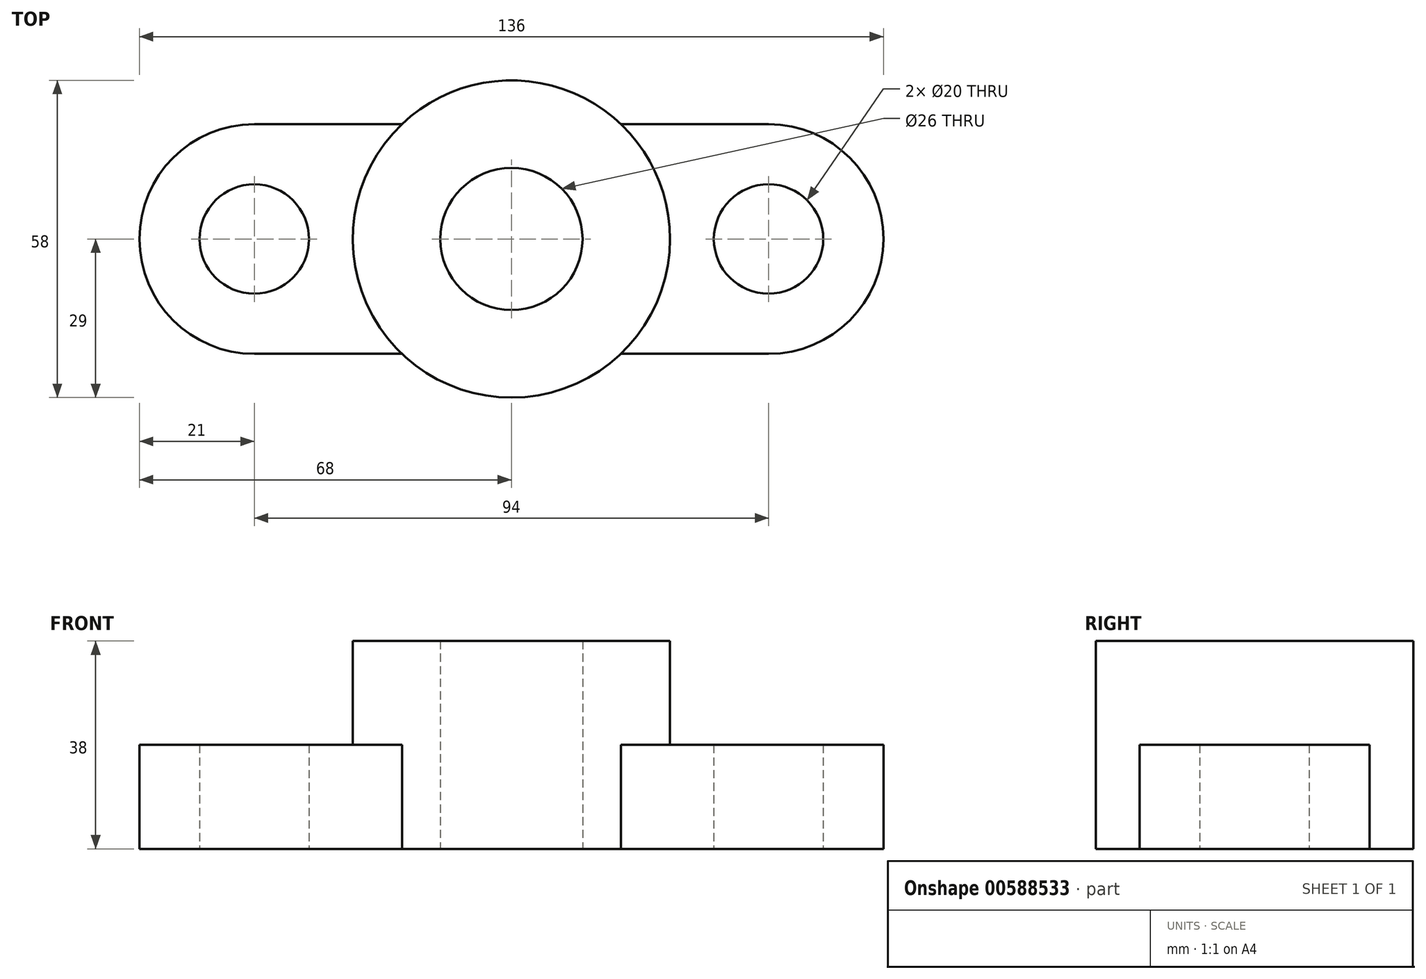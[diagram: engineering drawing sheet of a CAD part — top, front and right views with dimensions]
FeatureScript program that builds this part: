
annotation { "Feature Type Name" : "Feature", "Feature Type Description" : "" }
export const myFeature = defineFeature(function(context is Context, id is Id, definition is map)
    precondition{}
    {
        {
            var Q0;
            Q0=qCreatedBy(makeId("Top.planeOp"),FACE);
            var sketch = newSketch(context, id + "F0", { "sketchPlane" : qUnion([Q0])});
            skCircle(sketch, "E0", {"center": v(0, 0) * mm, "radius": 29 * mm});
            skPoint(sketch, "E1.center.orphan", {"position": v(-47, 0) * mm});
            skPoint(sketch, "E2.start.orphan", {"position": v(47, -11) * mm});
            skPoint(sketch, "E3.start.orphan", {"position": v(47, 11) * mm});
            skPoint(sketch, "E4.center.orphan", {"position": v(47, 0) * mm});
            skArc(sketch, "E5", {"start": v(-47, 21) * mm, "mid": v(-68, 0) * mm, "end": v(-47, -21) * mm});
            skArc(sketch, "E6", {"start": v(47, -21) * mm, "mid": v(68, 0) * mm, "end": v(47, 21) * mm});
            skLineSegment(sketch, "E7", {"start": v(-47, -21) * mm, "end": v(-20, -21) * mm});
            skLineSegment(sketch, "E8", {"start": v(-47, 21) * mm, "end": v(-20, 21) * mm});
            skLineSegment(sketch, "E9", {"start": v(47, 21) * mm, "end": v(20, 21) * mm});
            skLineSegment(sketch, "E10", {"start": v(47, -21) * mm, "end": v(20, -21) * mm});
            skCircle(sketch, "E11", {"center": v(-47, 0) * mm, "radius": 10 * mm});
            skCircle(sketch, "E12", {"center": v(47, 0) * mm, "radius": 10 * mm});
            skCircle(sketch, "E13", {"center": v(0, 0) * mm, "radius": 13 * mm});
            skSolve(sketch);
        }
        {
            var Q0;
            {var subQ0=sQuery(id+"F0.wireOp",EDGE,"E0");var subQ1=makeQuery(id+"F0.imprint","INTERSECT",VERTEX,{"derivedFrom":[subQ0,sQuery(id+"F0.wireOp",EDGE,"E8")]});Q0=makeQuery(id+"F0.imprint","IMPRINT",FACE,{"disambiguationData":[TD([[makeQuery(id+"F0.imprint","IMPRINT",EDGE,{"disambiguationData":[TD([[subQ1,1.0]])],"derivedFrom":subQ0}),1.0]])]});}
            extrude(context, id + "F1", {"entities" : qUnion([Q0]), "depth" : 38 * mm, "offsetDistance" : 25 * mm});
        }
        {
            var Q0;
            Q0 = qSketchRegion(id + "F0", true);
            extrude(context, id + "F2", {"entities" : qUnion([Q0]), "operationType" : NewBodyOperationType.ADD, "depth" : 19 * mm, "offsetDistance" : 25 * mm});
        }
    });
